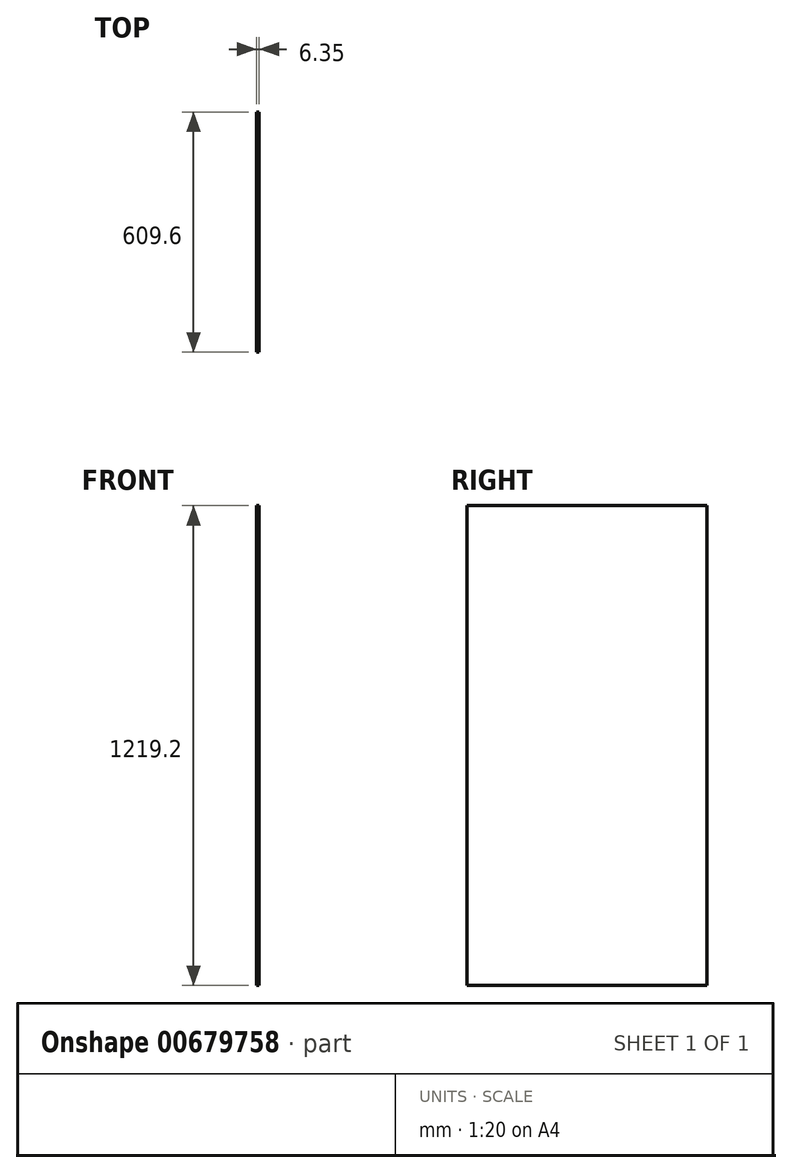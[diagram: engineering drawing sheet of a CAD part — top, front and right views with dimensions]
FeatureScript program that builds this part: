
annotation { "Feature Type Name" : "Feature", "Feature Type Description" : "" }
export const myFeature = defineFeature(function(context is Context, id is Id, definition is map)
    precondition{}
    {
        {
            var Q0;
            Q0=qCreatedBy(makeId("Right.planeOp"),FACE);
            var sketch = newSketch(context, id + "F0", { "sketchPlane" : qUnion([Q0])});
            skLineSegment(sketch, "E0.bottom", {"start": v(304.8, -609.6) * mm, "end": v(-304.8, -609.6) * mm});
            skLineSegment(sketch, "E0.top", {"start": v(304.8, 609.6) * mm, "end": v(-304.8, 609.6) * mm});
            skLineSegment(sketch, "E0.left", {"start": v(304.8, -609.6) * mm, "end": v(304.8, 609.6) * mm});
            skLineSegment(sketch, "E0.right", {"start": v(-304.8, -609.6) * mm, "end": v(-304.8, 609.6) * mm});
            skPoint(sketch, "E0.middle", {"position": v(0, 0) * mm});
            skSolve(sketch);
        }
        {
            var Q0;
            Q0 = qSketchRegion(id + "F0", true);
            extrude(context, id + "F1", {"entities" : qUnion([Q0]), "depth" : 6.35 * mm, "offsetDistance" : 30.48 * mm});
        }
    });
